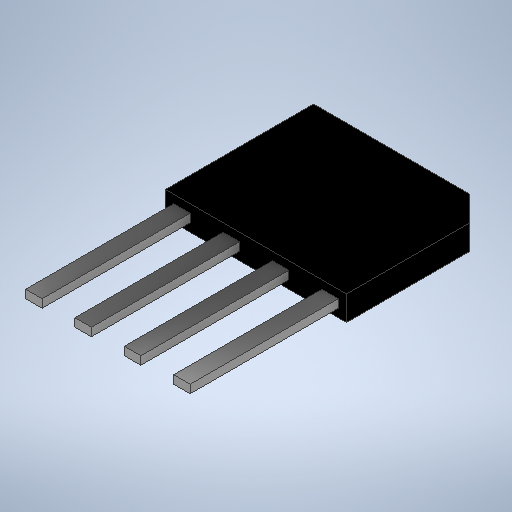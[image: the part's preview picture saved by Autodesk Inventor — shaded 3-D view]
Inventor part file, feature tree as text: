
AUTODESK INVENTOR PART (.ipt)
format: ipt  version: 2025.2 (Build 292293000, 293)  size: 287,232 bytes
history: native  units: mm
features: extrude x3, sketch x3
ambient origin geometry x8: Origin, YZ Plane, XZ Plane, XY Plane, X Axis, Y Axis, Z Axis, Center Point
bodies: Solid1 (feature_tree)
feature tree (6):
  extrude  "Extrusion1"  Depth=18.0mm
  extrude  "Extrusion2"  Depth=1.0mm
  extrude  "Extrusion3"  Depth=2.0mm
  sketch  "Sketch1"  dims[d0=22.0mm d1=18.0mm]
  sketch  "Sketch2"  dims[d2=3.0mm d3=0.0mm d4=1.0mm]
  sketch  "Sketch3"  dims[d5=1.0mm d6=2.0mm d7=1.0mm d8=1.0mm d9=2.0mm d10=1.0mm d11=2.0mm d12=1.0mm d13=2.0mm d14=1.0mm d15=1.0mm d16=1.0mm d17=1.0mm d18=4.0mm d19=4.0mm d20=18.0mm d21=0.0mm d22=3.0mm d23=3.0mm d24=18.0mm d25=0.0mm]
